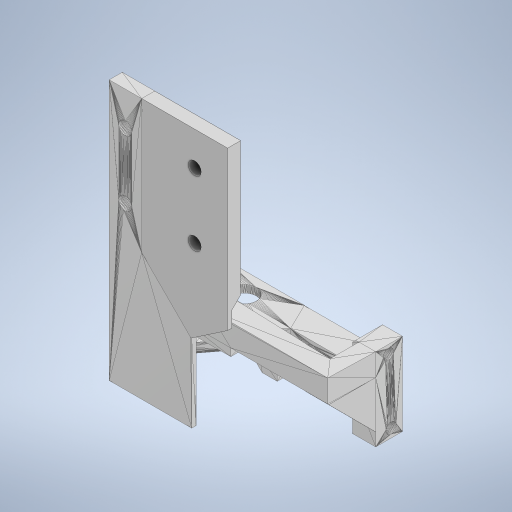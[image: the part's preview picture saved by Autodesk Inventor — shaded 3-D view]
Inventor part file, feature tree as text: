
AUTODESK INVENTOR PART (.ipt)
format: ipt  version: 2024.2 (Build 282272000, 272)  size: 311,808 bytes
history: native  units: mm
features: other x3, extrude x3, sketch x2, chamfer x1
ambient origin geometry x8: Origin, YZ Plane, XZ Plane, XY Plane, X Axis, Y Axis, Z Axis, Center Point
bodies: Body1 (feature_tree)
feature tree (9):
  other  "Твердое тело1"
  other  "крепежная основа"
  extrude  "Выдавливание1"  Depth=5.358mm TaperAngle=0.0deg
  sketch  "Эскиз2"
  extrude  "Выдавливание2"  Depth=3.0mm
  extrude  "Выдавливание3"  Depth=3.0mm
  chamfer  "Фаска1"  Distance=16.0mm
  sketch  "Эскиз1"
  other  "ЭлементСетки1"
